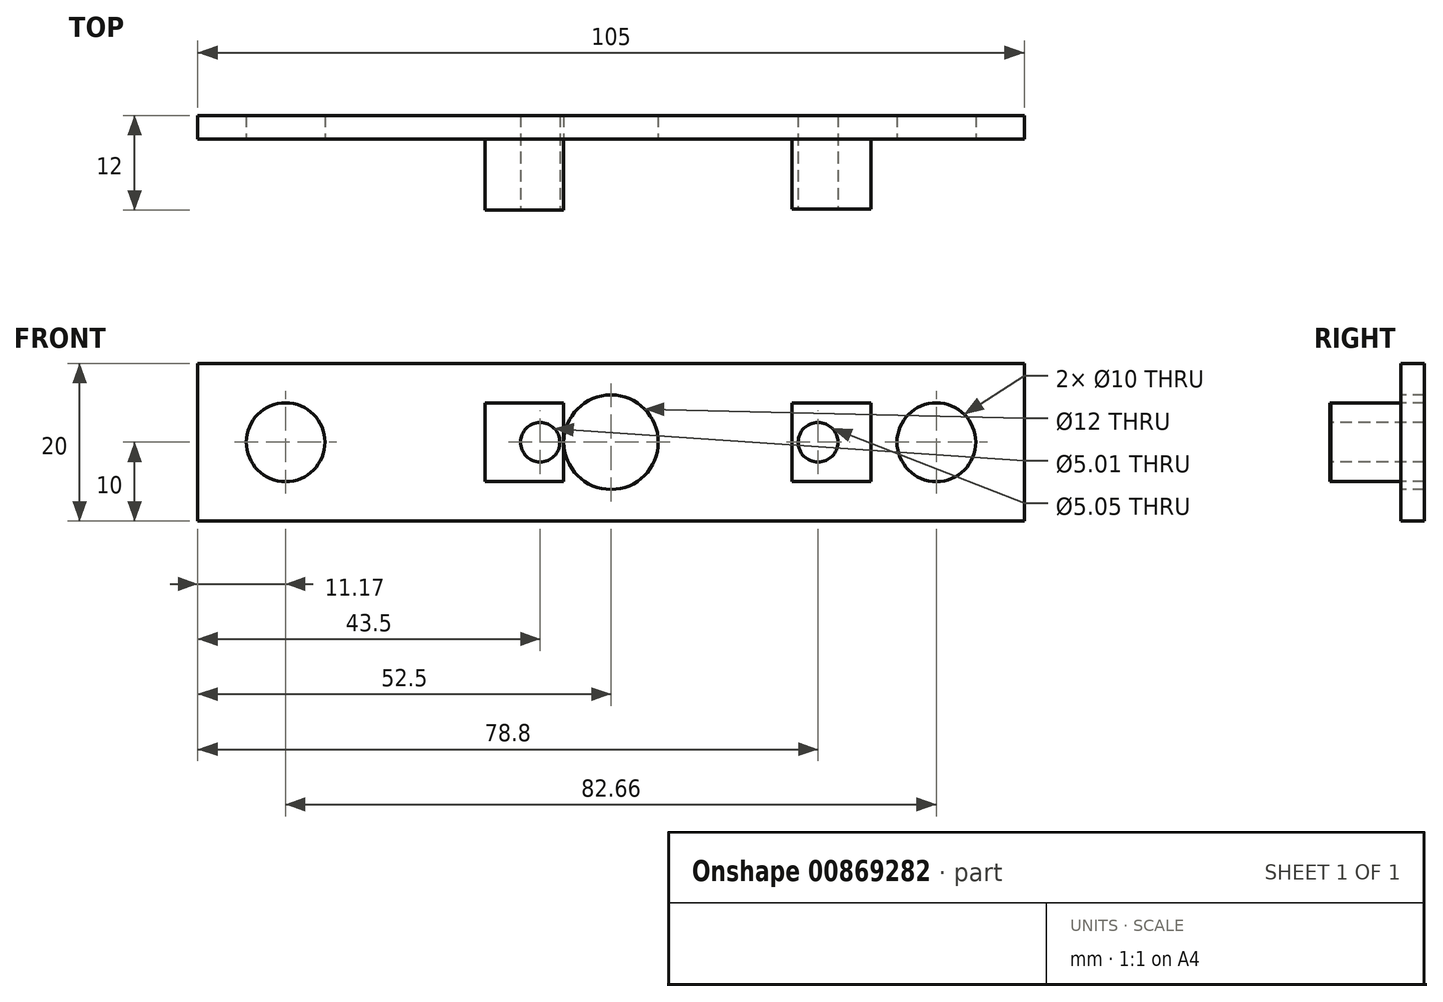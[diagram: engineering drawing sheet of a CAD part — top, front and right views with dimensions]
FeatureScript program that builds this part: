
annotation { "Feature Type Name" : "Feature", "Feature Type Description" : "" }
export const myFeature = defineFeature(function(context is Context, id is Id, definition is map)
    precondition{}
    {
        {
            var Q0;
            Q0=qCreatedBy(makeId("Front.planeOp"),FACE);
            var sketch = newSketch(context, id + "F0", { "sketchPlane" : qUnion([Q0])});
            skLineSegment(sketch, "E0.bottom", {"start": v(52.5, -10) * mm, "end": v(-52.5, -10) * mm});
            skLineSegment(sketch, "E0.top", {"start": v(52.5, 10) * mm, "end": v(-52.5, 10) * mm});
            skLineSegment(sketch, "E0.left", {"start": v(52.5, -10) * mm, "end": v(52.5, 10) * mm});
            skLineSegment(sketch, "E0.right", {"start": v(-52.5, -10) * mm, "end": v(-52.5, 10) * mm});
            skPoint(sketch, "E0.middle", {"position": v(0, 0) * mm});
            skSolve(sketch);
        }
        {
            var Q0;
            Q0 = qSketchRegion(id + "F0", true);
            extrude(context, id + "F1", {"entities" : qUnion([Q0]), "depth" : 3 * mm, "offsetDistance" : 25 * mm});
        }
        {
            var Q0;
            Q0=makeQuery(id+"F1.opExtrude","CAP_FACE",FACE,{"disambiguationData":[OSD([sQuery(id+"F0.wireOp",EDGE,"E0.bottom"),sQuery(id+"F0.wireOp",EDGE,"E0.top"),sQuery(id+"F0.wireOp",EDGE,"E0.left"),sQuery(id+"F0.wireOp",EDGE,"E0.right")])],"isStart":false});
            var sketch = newSketch(context, id + "F2", { "sketchPlane" : qUnion([Q0])});
            skCircle(sketch, "E1", {"center": v(0, 0) * mm, "radius": 6 * mm});
            skCircle(sketch, "E2", {"center": v(-41.33, 0) * mm, "radius": 5 * mm});
            skCircle(sketch, "E3", {"center": v(41.33, 0) * mm, "radius": 5 * mm});
            skSolve(sketch);
        }
        {
            var Q0;
            Q0 = qSketchRegion(id + "F2", true);
            extrude(context, id + "F3", {"entities" : qUnion([Q0]), "operationType" : NewBodyOperationType.REMOVE, "oppositeDirection" : true, "depth" : 25 * mm, "offsetDistance" : 25 * mm});
        }
        {
            var Q0;
            Q0=makeQuery(id+"F1.opExtrude","CAP_FACE",FACE,{"disambiguationData":[OSD([sQuery(id+"F0.wireOp",EDGE,"E0.bottom"),sQuery(id+"F0.wireOp",EDGE,"E0.top"),sQuery(id+"F0.wireOp",EDGE,"E0.left"),sQuery(id+"F0.wireOp",EDGE,"E0.right")])],"isStart":false});
            var sketch = newSketch(context, id + "F4", { "sketchPlane" : qUnion([Q0])});
            skLineSegment(sketch, "E4.bottom", {"start": v(-6, -5) * mm, "end": v(-16, -5) * mm});
            skLineSegment(sketch, "E4.top", {"start": v(-6, 5) * mm, "end": v(-16, 5) * mm});
            skLineSegment(sketch, "E4.left", {"start": v(-6, -5) * mm, "end": v(-6, 5) * mm});
            skLineSegment(sketch, "E4.right", {"start": v(-16, -5) * mm, "end": v(-16, 5) * mm});
            skPoint(sketch, "E4.middle", {"position": v(-11, 0) * mm});
            skSolve(sketch);
        }
        {
            var Q0;
            Q0=makeQuery(id+"F4.imprint","IMPRINT",FACE,{"disambiguationData":[TD([[makeQuery(id+"F4.imprint","IMPRINT",EDGE,{"derivedFrom":sQuery(id+"F4.wireOp",EDGE,"E4.bottom")}),1.0]])]});
            var sketch = newSketch(context, id + "F5", { "sketchPlane" : qUnion([Q0])});
            skLineSegment(sketch, "E5.bottom", {"start": v(33, 5) * mm, "end": v(23, 5) * mm});
            skLineSegment(sketch, "E5.top", {"start": v(33, -5) * mm, "end": v(23, -5) * mm});
            skLineSegment(sketch, "E5.left", {"start": v(33, 5) * mm, "end": v(33, -5) * mm});
            skLineSegment(sketch, "E5.right", {"start": v(23, 5) * mm, "end": v(23, -5) * mm});
            skPoint(sketch, "E5.middle", {"position": v(28, 0) * mm});
            skSolve(sketch);
        }
        {
            var Q0;
            Q0=makeQuery(id+"F5.imprint","IMPRINT",FACE,{"disambiguationData":[TD([[makeQuery(id+"F5.imprint","IMPRINT",EDGE,{"derivedFrom":sQuery(id+"F5.wireOp",EDGE,"E5.bottom")}),1.0]])]});
            extrude(context, id + "F6", {"entities" : qUnion([Q0]), "operationType" : NewBodyOperationType.ADD, "depth" : 8.9 * mm, "offsetDistance" : 25 * mm});
        }
        {
            var Q0;
            Q0=makeQuery(id+"F4.imprint","IMPRINT",FACE,{"disambiguationData":[TD([[makeQuery(id+"F4.imprint","IMPRINT",EDGE,{"derivedFrom":sQuery(id+"F4.wireOp",EDGE,"E4.bottom")}),-1.0]])]});
            extrude(context, id + "F7", {"entities" : qUnion([Q0]), "operationType" : NewBodyOperationType.ADD, "depth" : 9 * mm, "offsetDistance" : 25 * mm});
        }
        {
            var Q0;
            Q0=makeQuery(id+"F7.opExtrude","CAP_FACE",FACE,{"disambiguationData":[OSD([sQuery(id+"F4.wireOp",EDGE,"E4.bottom"),sQuery(id+"F4.wireOp",EDGE,"E4.top"),sQuery(id+"F4.wireOp",EDGE,"E4.left"),sQuery(id+"F4.wireOp",EDGE,"E4.right")])],"isStart":false});
            var sketch = newSketch(context, id + "F8", { "sketchPlane" : qUnion([Q0])});
            skCircle(sketch, "E6", {"center": v(-9, 0) * mm, "radius": 2.5 * mm});
            skCircle(sketch, "E7", {"center": v(26.3, 0) * mm, "radius": 2.52 * mm});
            skSolve(sketch);
        }
        {
            var Q0;
            Q0 = qSketchRegion(id + "F8", true);
            extrude(context, id + "F9", {"entities" : qUnion([Q0]), "operationType" : NewBodyOperationType.REMOVE, "oppositeDirection" : true, "depth" : 25 * mm, "offsetDistance" : 25 * mm});
        }
    });
